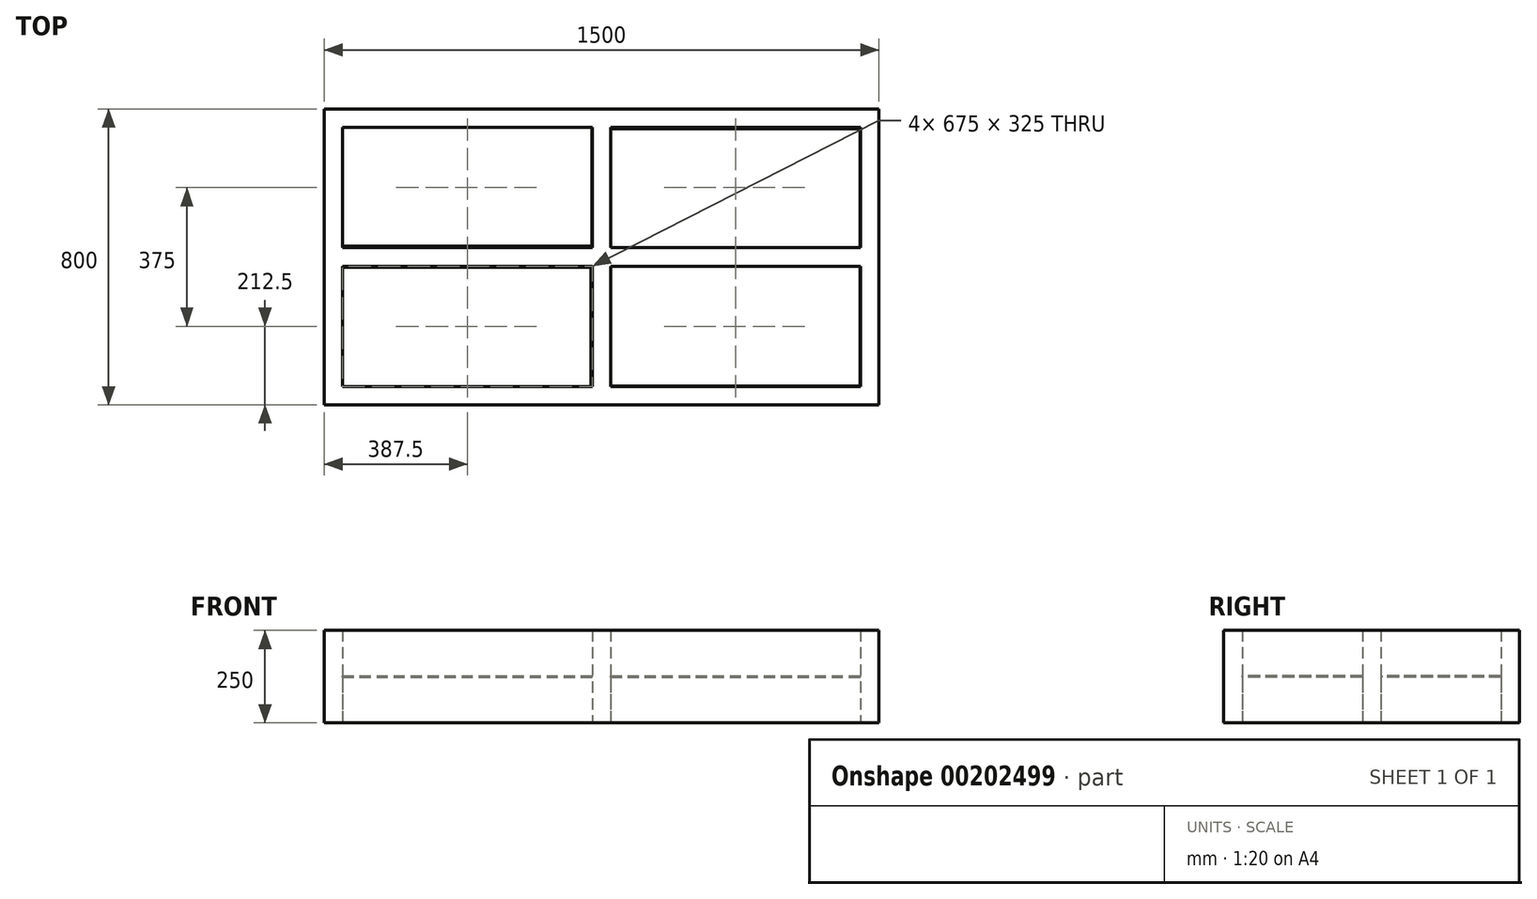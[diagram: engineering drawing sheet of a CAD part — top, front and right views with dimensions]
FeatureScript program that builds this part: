
annotation { "Feature Type Name" : "Feature", "Feature Type Description" : "" }
export const myFeature = defineFeature(function(context is Context, id is Id, definition is map)
    precondition{}
    {
        {
            var Q0;
            Q0=qCreatedBy(makeId("Top.planeOp"),FACE);
            var sketch = newSketch(context, id + "F0", { "sketchPlane" : qUnion([Q0])});
            skLineSegment(sketch, "E0.bottom", {"start": v(750, 400) * mm, "end": v(-750, 400) * mm});
            skLineSegment(sketch, "E0.top", {"start": v(750, -400) * mm, "end": v(-750, -400) * mm});
            skLineSegment(sketch, "E0.left", {"start": v(750, 400) * mm, "end": v(750, -400) * mm});
            skLineSegment(sketch, "E0.right", {"start": v(-750, 400) * mm, "end": v(-750, -400) * mm});
            skPoint(sketch, "E0.middle", {"position": v(0, 0) * mm});
            skLineSegment(sketch, "E1.bottom", {"start": v(-700, 350) * mm, "end": v(-25, 350) * mm});
            skLineSegment(sketch, "E1.top", {"start": v(-700, 25) * mm, "end": v(-25, 25) * mm});
            skLineSegment(sketch, "E1.left", {"start": v(-700, 350) * mm, "end": v(-700, 25) * mm});
            skLineSegment(sketch, "E1.right", {"start": v(-25, 350) * mm, "end": v(-25, 25) * mm});
            skLineSegment(sketch, "E2.bottom", {"start": v(-700, -25) * mm, "end": v(-25, -25) * mm});
            skLineSegment(sketch, "E2.top", {"start": v(-700, -350) * mm, "end": v(-25, -350) * mm});
            skLineSegment(sketch, "E2.left", {"start": v(-700, -25) * mm, "end": v(-700, -350) * mm});
            skLineSegment(sketch, "E2.right", {"start": v(-25, -25) * mm, "end": v(-25, -350) * mm});
            skLineSegment(sketch, "E3.bottom", {"start": v(25, 350) * mm, "end": v(700, 350) * mm});
            skLineSegment(sketch, "E3.top", {"start": v(25, 25) * mm, "end": v(700, 25) * mm});
            skLineSegment(sketch, "E3.left", {"start": v(25, 350) * mm, "end": v(25, 25) * mm});
            skLineSegment(sketch, "E3.right", {"start": v(700, 350) * mm, "end": v(700, 25) * mm});
            skLineSegment(sketch, "E4.bottom", {"start": v(25, -25) * mm, "end": v(700, -25) * mm});
            skLineSegment(sketch, "E4.top", {"start": v(25, -350) * mm, "end": v(700, -350) * mm});
            skLineSegment(sketch, "E4.left", {"start": v(25, -25) * mm, "end": v(25, -350) * mm});
            skLineSegment(sketch, "E4.right", {"start": v(700, -25) * mm, "end": v(700, -350) * mm});
            skSolve(sketch);
        }
        {
            var Q0;
            Q0=makeQuery(id+"F0.imprint","IMPRINT",FACE,{"disambiguationData":[TD([[makeQuery(id+"F0.imprint","IMPRINT",EDGE,{"derivedFrom":sQuery(id+"F0.wireOp",EDGE,"E0.bottom")}),1.0]])]});
            extrude(context, id + "F1", {"entities" : qUnion([Q0]), "endBound" : BoundingType.SYMMETRIC, "depth" : 250 * mm});
        }
        {
            var Q0;
            Q0=qCreatedBy(makeId("Top.planeOp"),FACE);
            var sketch = newSketch(context, id + "F2", { "sketchPlane" : qUnion([Q0])});
            skLineSegment(sketch, "E5.bottom", {"start": v(-701.09, 353.53) * mm, "end": v(-26.09, 353.53) * mm});
            skLineSegment(sketch, "E5.top", {"start": v(-701.09, 28.53) * mm, "end": v(-26.09, 28.53) * mm});
            skLineSegment(sketch, "E5.left", {"start": v(-701.09, 353.53) * mm, "end": v(-701.09, 28.53) * mm});
            skLineSegment(sketch, "E5.right", {"start": v(-26.09, 353.53) * mm, "end": v(-26.09, 28.53) * mm});
            skLineSegment(sketch, "E6.bottom", {"start": v(-702.72, -27.99) * mm, "end": v(-27.72, -27.99) * mm});
            skLineSegment(sketch, "E6.top", {"start": v(-702.72, -352.99) * mm, "end": v(-27.72, -352.99) * mm});
            skLineSegment(sketch, "E6.left", {"start": v(-702.72, -27.99) * mm, "end": v(-702.72, -352.99) * mm});
            skLineSegment(sketch, "E6.right", {"start": v(-27.72, -27.99) * mm, "end": v(-27.72, -352.99) * mm});
            skLineSegment(sketch, "E7.bottom", {"start": v(24.46, 347.01) * mm, "end": v(699.46, 347.01) * mm});
            skLineSegment(sketch, "E7.top", {"start": v(24.46, 22.01) * mm, "end": v(699.46, 22.01) * mm});
            skLineSegment(sketch, "E7.left", {"start": v(24.46, 347.01) * mm, "end": v(24.46, 22.01) * mm});
            skLineSegment(sketch, "E7.right", {"start": v(699.46, 347.01) * mm, "end": v(699.46, 22.01) * mm});
            skLineSegment(sketch, "E8.bottom", {"start": v(24.46, -24.73) * mm, "end": v(699.46, -24.73) * mm});
            skLineSegment(sketch, "E8.top", {"start": v(24.46, -349.73) * mm, "end": v(699.46, -349.73) * mm});
            skLineSegment(sketch, "E8.left", {"start": v(24.46, -24.73) * mm, "end": v(24.46, -349.73) * mm});
            skLineSegment(sketch, "E8.right", {"start": v(699.46, -24.73) * mm, "end": v(699.46, -349.73) * mm});
            skSolve(sketch);
        }
        {
            var Q0;
            Q0=makeQuery(id+"F2.imprint","IMPRINT",FACE,{"disambiguationData":[TD([[makeQuery(id+"F2.imprint","IMPRINT",EDGE,{"derivedFrom":sQuery(id+"F2.wireOp",EDGE,"E5.bottom")}),-1.0]])]});
            var Q1;
            Q1=makeQuery(id+"F2.imprint","IMPRINT",FACE,{"disambiguationData":[TD([[makeQuery(id+"F2.imprint","IMPRINT",EDGE,{"derivedFrom":sQuery(id+"F2.wireOp",EDGE,"E7.bottom")}),-1.0]])]});
            var Q2;
            Q2=makeQuery(id+"F2.imprint","IMPRINT",FACE,{"disambiguationData":[TD([[makeQuery(id+"F2.imprint","IMPRINT",EDGE,{"derivedFrom":sQuery(id+"F2.wireOp",EDGE,"E6.bottom")}),-1.0]])]});
            var Q3;
            Q3=makeQuery(id+"F2.imprint","IMPRINT",FACE,{"disambiguationData":[TD([[makeQuery(id+"F2.imprint","IMPRINT",EDGE,{"derivedFrom":sQuery(id+"F2.wireOp",EDGE,"E8.bottom")}),-1.0]])]});
            extrude(context, id + "F3", {"entities" : qUnion([Q0, Q1, Q2, Q3]), "operationType" : NewBodyOperationType.ADD, "endBound" : BoundingType.SYMMETRIC, "depth" : 3 * mm});
        }
    });
